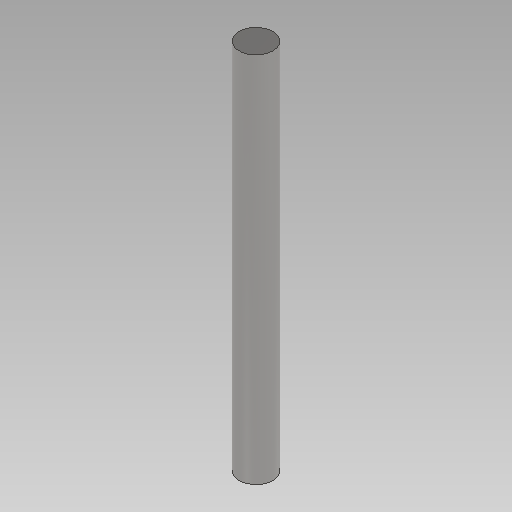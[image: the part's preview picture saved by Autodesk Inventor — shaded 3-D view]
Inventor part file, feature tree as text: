
AUTODESK INVENTOR PART (.ipt)
format: ipt  version: 2020 (Build 240168000, 168)  size: 86,528 bytes
history: native  units: in
note: dims shown in document units (in); Inventor stores cm internally (conversion verified against a paired STEP export)
features: extrude x1, sketch x1
ambient origin geometry x8: Origin, YZ Plane, XZ Plane, XY Plane, X Axis, Y Axis, Z Axis, Center Point
bodies: Solid1 (feature_tree)
feature tree (2):
  extrude  "Extrusion1"  Depth=4.3307in TaperAngle=0.0deg
  sketch  "Sketch1"  dims[d0=0.3937in d1=4.3307in d2=0.0in]
